# Revit family: PRD_FrankeWS_ShwrMxrs_SelfClosingShowerMixer_F5SM2004,2005_V1
name_source: partatom
category: Plumbing Fixtures
revit_build: Autodesk Revit 2018 (Build: 20190510_1515(x64)
units: mm (PartAtom-declared; Revit-internal decimal feet)

## family parameters
Cut with Voids When Loaded = Yes
Host = Face
OmniClass Number = 23.45.05.14.99
OmniClass Title = Other Sanitary Washing Plumbing Fixtures
Part Type = Normal
Room Calculation Point = No
Round Connector Dimension = Use Diameter
Shared = No

## types (2) — shared parameters
AdditionalConnections = no
AdjustableFlowTime = yes
AssetType = Fixed
CasingMaterial = PRD_AR_StainlessSteel_SatinFinished
Category = Pr_40_20_87_78, Shower manual water supply sets
Circulation = no
CloseOffRating = 0.0 Pa
Color = satin finished
ConnectionWithPayWaterDispenser = not possible
Default Elevation = 850 mm  [stored 2.78871 ft]
DiameterNominal = 15  [stored 0.0492126 ft]
DurationUnit = year
FaucetMaterial = PRD_AR_ChromatedBrass_HighPolished
Features = For shower facilities, connects to hot and cold water. Stainless steel cover plate 190 x 245 mm.
Finish = high-polished chromium-plated brass
FlowCoefficient = 0
FlowColdWater = 0.2 L/s
FlowHotWater = 0.2 L/s
FunctionalPrinciple = hydraulic self-closing
HygieneFlushing = no
IfcExportAs = IfcValveType
IfcExportType = MIXING
InletSize = G-3-4-B
Manufacturer = KWC Group AG
ManufacturerName = KWC Group AG
ManufacturerURL = www.kwc.com
Material = stainless steel
MaterialsBody = Brass
MaximumFlowTime = 35.00 seconds
MinimumFlowPressure = 0.50 bar
MinimumFlowTime = 5.00 seconds
MixerControl = Other
NBSDescription = Shower manual water supply sets
NBSReference = 45-35-70/335
NominalHeight = 245 mm  [stored 0.803806 ft]
NominalWidth = 190 mm  [stored 0.62336 ft]
OutletConnectionSize = 15 mm  [stored 0.0492126 ft]
PositionOfWaterConnection = from side
ProductInformation = https://pim.kwc.com
ProtectiveShutdown = no
SoundInsulation = no
TestPressure = 0.0 Pa
ThermalDisinfection = no
TypeOfMixing = with mixer
TypeOfMounting = in-wall installation with box
TypeOfOperation = manual operation
TypeOfShower = in-wall fitting
URL = www.kwc.com
Uniclass2015Code = Pr_40_20_87_78
Uniclass2015Title = Shower manual water supply sets
Uniclass2015Version = Products v1.10
ValveMechanism = Other
ValveOperation = Other
ValvePattern = ANGLED_2_PORT
Version = 1
VolumeFlowRate = 0.20 L/s at 3 bar
WarrantyDurationUnit = year
zero-valued in all types: NominalLength

## per-type parameters (varying)
| type | BIMObjectName | Description | GrossWeight | Model | ModelNumber | ModelReference | Name | NetWeight | ShowerPipeDraining | ShowerPipeDrainingVisibility |
| F5SM2004 - 0.20 L/s, | PRD_AR_ShowerMixers_SelfClosingShowerMixer_F5SM2004 | F5S-Mix self-closing single-mixer DN 15 as finished installation kit for installation in basic installation kit, for shower facilities. FRAMIC self-closing mixing cartridge, hydraulically controlled, low-maintenance and stagnation-free, with ceramic disc technology, self-closing, flow pressure-independent due to medium-separated design. Stepless adjustment of flow duration. With adjustable, turn-proof temperature stop. Connects to hot and cold water. All-metal construction, visible parts high-polished, chromium-plated. Holding frame including profile seal, stainless steel cover plate 190 x 245 mm with covered screw fixing, chromium-plated plastic rosettes, backflow preventer and strainers. Depth adjustability 25 mm. | 3.05 kg | F5SM2004 | 2030029012 | F5SM2004 | F5 self-closing shower mixer F5SM2004 | 2.75 kg | no | No |
| F5SM2005 - 0.20 L/s, with automatic shower pipe draining | PRD_AR_ShowerMixers_SelfClosingShowerMixer_F5SM2005 | F5S-Mix self-closing single-mixer DN 15 as finished installation kit for installation in basic installation kit, for shower facilities. FRAMIC self-closing mixing cartridge, hydraulically controlled, low-maintenance and stagnation-free, with ceramic disc technology, self-closing, flow pressure-independent due to medium-separated design. Stepless adjustment of flow duration. With adjustable, turn-proof temperature stop. Connects to hot and cold water. All-metal construction, visible parts high-polished, chromium-plated. Holding frame including profile seal, stainless steel cover plate 190 x 245 mm with covered screw fixing, chromium-plated plastic rosettes, backflow preventer and strainers. Depth adjustability 25 mm. Version with automatic shower pipe draining. | 3.20 kg | F5SM2005 | 2030036693 | F5SM2005 | F5 self-closing shower mixer F5SM2005 | 3.00 kg | yes | Yes |

note: [stored X ft] marks values corroborated as IEEE doubles in the binary element streams (Revit-internal decimal feet)

## geometry (parser evidence)
native form markers: Sweep x4
no freeform markers — native parametric forms only
